# Revit family: M_Level Valve - 65-80 mm - Flanged
name_source: partatom
category: Pipe Accessories
revit_build: Autodesk Revit 2014 (Build: 20130308_1515(x64)
units: mm (PartAtom-declared; Revit-internal decimal feet)

## types (2) — shared parameters
Handle = Paint - Red
Valve Material = PVC, Green

## per-type parameters (varying)
| type | Body Diameter | Body Radius | Bonnet Length | Bottom Radius | Flange Diameter | Flange Radius | Flange Thickness | H2 | H3 | Half Bonnet Length | Height 1 | Height 2 | Height 3 | K Coefficient | Nominal Radius | Outside Diameter | Outside Radius | Radius 1 | Valve Length |
| 65 mm | 158 mm | 79 mm | 118 mm | 26 mm | 178 mm  [stored 0.58399 ft] | 89 mm  [stored 0.291995 ft] | 11 mm | 131 mm | 39 mm | 59 mm | 102 mm | 124 mm  [stored 0.406824 ft] | 25 mm | 7.09 | 33 mm | 91 mm  [stored 0.298556 ft] | 46 mm | 13 mm | 197 mm |
| 80 mm | 183 mm | 92 mm | 137 mm | 31 mm | 203 mm  [stored 0.66601 ft] | 102 mm | 13 mm | 153 mm | 46 mm | 69 mm | 108 mm  [stored 0.354331 ft] | 129 mm  [stored 0.423228 ft] | 26 mm | 7.21 | 40 mm | 112 mm  [stored 0.367454 ft] | 56 mm  [stored 0.183727 ft] | 15 mm  [stored 0.0492126 ft] | 229 mm |

note: column(s) folded — value = type name in every type: Nominal Diameter

note: [stored X ft] marks values corroborated as IEEE doubles in the binary element streams (Revit-internal decimal feet)

## geometry (parser evidence)
native form markers: Sweep x2
no freeform markers — native parametric forms only
